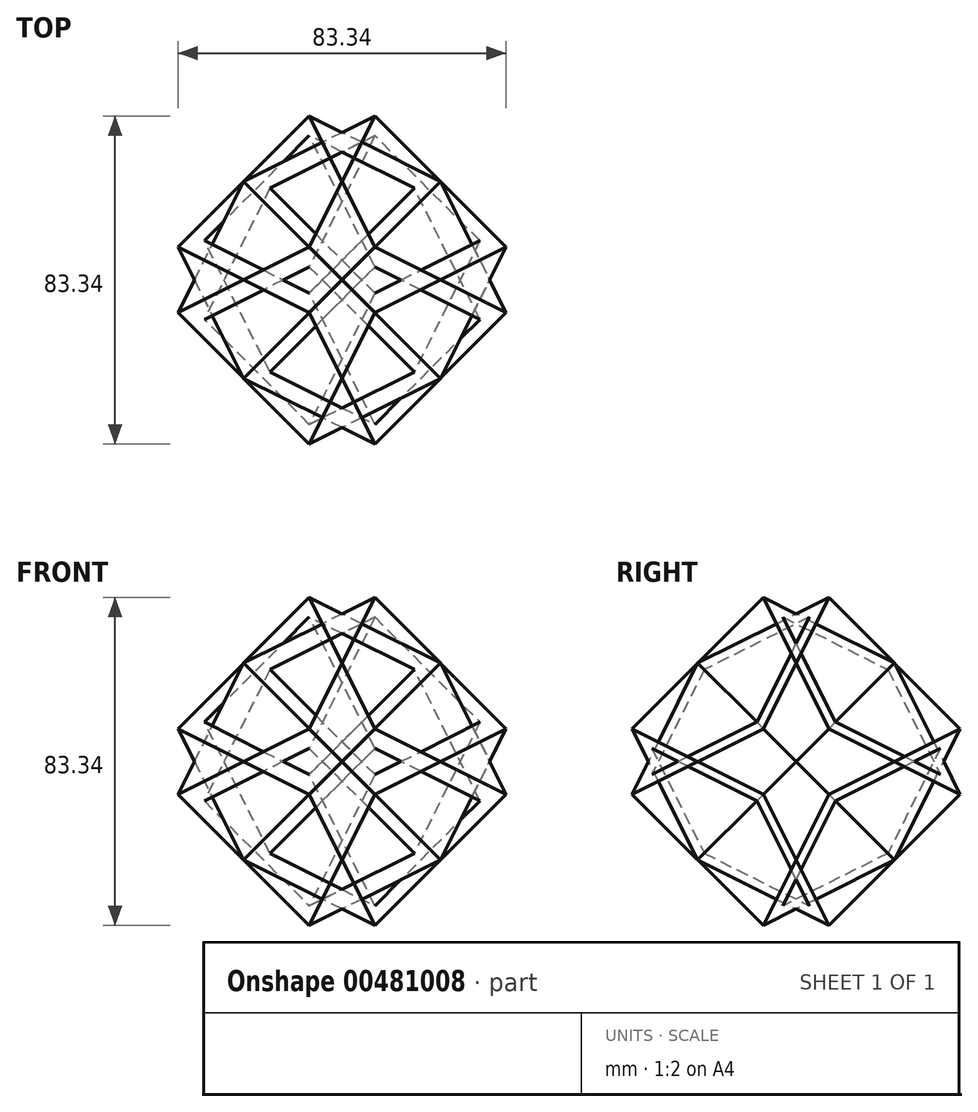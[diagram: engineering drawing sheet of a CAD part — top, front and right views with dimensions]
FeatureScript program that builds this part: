
annotation { "Feature Type Name" : "Feature", "Feature Type Description" : "" }
export const myFeature = defineFeature(function(context is Context, id is Id, definition is map)
    precondition{}
    {
        {
            var Q0;
            Q0=qCreatedBy(makeId("Front.planeOp"),FACE);
            var sketch = newSketch(context, id + "F0", { "sketchPlane" : qUnion([Q0])});
            skLineSegment(sketch, "E0.bottom", {"start": v(25, 25) * mm, "end": v(-25, 25) * mm});
            skLineSegment(sketch, "E0.top", {"start": v(25, -25) * mm, "end": v(-25, -25) * mm});
            skLineSegment(sketch, "E0.left", {"start": v(25, 25) * mm, "end": v(25, -25) * mm});
            skLineSegment(sketch, "E0.right", {"start": v(-25, 25) * mm, "end": v(-25, -25) * mm});
            skPoint(sketch, "E0.middle", {"position": v(0, 0) * mm});
            skSolve(sketch);
        }
        {
            var Q0;
            Q0=makeQuery(id+"F0.imprint","IMPRINT",FACE,{"disambiguationData":[TD([[makeQuery(id+"F0.imprint","IMPRINT",EDGE,{"derivedFrom":sQuery(id+"F0.wireOp",EDGE,"E0.bottom")}),1.0]])]});
            extrude(context, id + "F1", {"entities" : qUnion([Q0]), "endBound" : BoundingType.SYMMETRIC, "depth" : 50 * mm});
        }
        {
            var Q0;
            Q0=makeQuery(id+"F1.opExtrude","CAP_VERTEX",VERTEX,{"disambiguationData":[OSD([sQuery(id+"F0.wireOp",EDGE,"E0.bottom"),sQuery(id+"F0.wireOp",EDGE,"E0.left")])],"isStart":false});
            var Q1;
            Q1=makeQuery(id+"F1.opExtrude","CAP_VERTEX",VERTEX,{"disambiguationData":[OSD([sQuery(id+"F0.wireOp",EDGE,"E0.top"),sQuery(id+"F0.wireOp",EDGE,"E0.left")])],"isStart":false});
            var Q2;
            Q2=makeQuery(id+"F1.opExtrude","CAP_VERTEX",VERTEX,{"disambiguationData":[OSD([sQuery(id+"F0.wireOp",EDGE,"E0.top"),sQuery(id+"F0.wireOp",EDGE,"E0.right")])],"isStart":true});
            cPlane(context, id + "F2", {"entities" : qUnion([Q0, Q1, Q2]), "cplaneType" : CPlaneType.THREE_POINT, "offset" : 25 * mm, "width" : 150 * mm, "height" : 150 * mm});
        }
        {
            var Q0;
            Q0=qCreatedBy(id+"F2.planeOp",FACE);
            var sketch = newSketch(context, id + "F3", { "sketchPlane" : qUnion([Q0])});
            skLineSegment(sketch, "E1", {"start": v(-46.2, -32.67) * mm, "end": v(57, 40.3) * mm, "construction": true});
            skSolve(sketch);
        }
        {
            var Q0;
            Q0=makeQuery(id+"F1.opExtrude","SWEPT_BODY",BODY,{"disambiguationData":[OSD([sQuery(id+"F0.wireOp",EDGE,"E0.bottom"),sQuery(id+"F0.wireOp",EDGE,"E0.top"),sQuery(id+"F0.wireOp",EDGE,"E0.left"),sQuery(id+"F0.wireOp",EDGE,"E0.right")])]});
            var Q1;
            Q1=sQuery(id+"F3.wireOp",EDGE,"E1");
            transform(context, id + "F4", {"entities" : qUnion([Q0]), "transformType" : TransformType.ROTATION, "transformAxis" : qUnion([Q1]), "angle" : 60 * degree, "makeCopy" : false});
        }
        {
            var Q0;
            Q0=qCreatedBy(makeId("Front.planeOp"),FACE);
            var sketch = newSketch(context, id + "F5", { "sketchPlane" : qUnion([Q0])});
            skLineSegment(sketch, "E2", {"start": v(-43.87, 0) * mm, "end": v(62.3, 0) * mm, "construction": true});
            skSolve(sketch);
        }
        {
            var Q0;
            Q0=makeQuery(id+"F1.opExtrude","SWEPT_BODY",BODY,{"disambiguationData":[OSD([sQuery(id+"F0.wireOp",EDGE,"E0.bottom"),sQuery(id+"F0.wireOp",EDGE,"E0.top"),sQuery(id+"F0.wireOp",EDGE,"E0.left"),sQuery(id+"F0.wireOp",EDGE,"E0.right")])]});
            var Q1;
            Q1=sQuery(id+"F5.wireOp",EDGE,"E2");
            transform(context, id + "F6", {"entities" : qUnion([Q0]), "transformType" : TransformType.ROTATION, "transformAxis" : qUnion([Q1]), "angle" : 90 * degree, "makeCopy" : true});
        }
        {
            var Q0;
            Q0=makeQuery(id+"F1.opExtrude","SWEPT_BODY",BODY,{"disambiguationData":[OSD([sQuery(id+"F0.wireOp",EDGE,"E0.bottom"),sQuery(id+"F0.wireOp",EDGE,"E0.top"),sQuery(id+"F0.wireOp",EDGE,"E0.left"),sQuery(id+"F0.wireOp",EDGE,"E0.right")])]});
            var Q1;
            Q1=sQuery(id+"F5.wireOp",EDGE,"E2");
            transform(context, id + "F7", {"entities" : qUnion([Q0]), "transformType" : TransformType.ROTATION, "transformAxis" : qUnion([Q1]), "angle" : 270 * degree, "makeCopy" : true});
        }
        {
            var Q0;
            Q0=makeQuery(id+"F1.opExtrude","SWEPT_BODY",BODY,{"disambiguationData":[OSD([sQuery(id+"F0.wireOp",EDGE,"E0.bottom"),sQuery(id+"F0.wireOp",EDGE,"E0.top"),sQuery(id+"F0.wireOp",EDGE,"E0.left"),sQuery(id+"F0.wireOp",EDGE,"E0.right")])]});
            var Q1;
            Q1=sQuery(id+"F5.wireOp",EDGE,"E2");
            transform(context, id + "F8", {"entities" : qUnion([Q0]), "transformType" : TransformType.ROTATION, "transformAxis" : qUnion([Q1]), "angle" : 180 * degree, "makeCopy" : true});
        }
        {
            var Q0;
            Q0=makeQuery(id+"F1.opExtrude","CAP_FACE",FACE,{"disambiguationData":[OSD([sQuery(id+"F0.wireOp",EDGE,"E0.bottom"),sQuery(id+"F0.wireOp",EDGE,"E0.top"),sQuery(id+"F0.wireOp",EDGE,"E0.left"),sQuery(id+"F0.wireOp",EDGE,"E0.right")])],"isStart":false});
            var sketch = newSketch(context, id + "F9", { "sketchPlane" : qUnion([Q0])});
            skLineSegment(sketch, "E3.0", {"start": v(8.94, -26.83) * mm, "end": v(26.83, 8.94) * mm});
            skLineSegment(sketch, "E3.1", {"start": v(-26.83, -8.94) * mm, "end": v(8.94, -26.83) * mm});
            skLineSegment(sketch, "E3.2", {"start": v(-8.94, 26.83) * mm, "end": v(-26.83, -8.94) * mm});
            skLineSegment(sketch, "E3.3", {"start": v(26.83, 8.94) * mm, "end": v(-8.94, 26.83) * mm});
            skSolve(sketch);
        }
        {
            var Q0;
            Q0=makeQuery(id+"F9.imprint","IMPRINT",FACE,{"disambiguationData":[TD([[makeQuery(id+"F9.imprint","IMPRINT",EDGE,{"derivedFrom":sQuery(id+"F9.wireOp",EDGE,"E3.0")}),1.0]])]});
            extrude(context, id + "F10", {"entities" : qUnion([Q0]), "operationType" : NewBodyOperationType.REMOVE, "endBound" : BoundingType.THROUGH_ALL, "oppositeDirection" : true, "depth" : 25 * mm});
        }
        {
            var Q0;
            Q0=makeQuery(id+"F1.opExtrude","SWEPT_FACE",FACE,{"disambiguationData":[OSD([sQuery(id+"F0.wireOp",EDGE,"E0.bottom")])]});
            var sketch = newSketch(context, id + "F11", { "sketchPlane" : qUnion([Q0])});
            skLineSegment(sketch, "E4.0", {"start": v(0, 28.28) * mm, "end": v(-28.28, 0) * mm});
            skLineSegment(sketch, "E4.1", {"start": v(28.28, 0) * mm, "end": v(0, 28.28) * mm});
            skLineSegment(sketch, "E4.2", {"start": v(0, -28.28) * mm, "end": v(28.28, 0) * mm});
            skLineSegment(sketch, "E4.3", {"start": v(-28.28, 0) * mm, "end": v(0, -28.28) * mm});
            skSolve(sketch);
        }
        {
            var Q0;
            Q0=makeQuery(id+"F11.imprint","IMPRINT",FACE,{"disambiguationData":[TD([[makeQuery(id+"F11.imprint","IMPRINT",EDGE,{"derivedFrom":sQuery(id+"F11.wireOp",EDGE,"E4.0")}),1.0]])]});
            extrude(context, id + "F12", {"entities" : qUnion([Q0]), "operationType" : NewBodyOperationType.REMOVE, "endBound" : BoundingType.THROUGH_ALL, "oppositeDirection" : true, "depth" : 25 * mm});
        }
        {
            var Q0;
            Q0=makeQuery(id+"F1.opExtrude","SWEPT_FACE",FACE,{"disambiguationData":[OSD([sQuery(id+"F0.wireOp",EDGE,"E0.left")])]});
            var sketch = newSketch(context, id + "F13", { "sketchPlane" : qUnion([Q0])});
            skLineSegment(sketch, "E5.0", {"start": v(-8.94, 26.83) * mm, "end": v(-26.83, -8.94) * mm});
            skLineSegment(sketch, "E5.1", {"start": v(26.83, 8.94) * mm, "end": v(-8.94, 26.83) * mm});
            skLineSegment(sketch, "E5.2", {"start": v(8.94, -26.83) * mm, "end": v(26.83, 8.94) * mm});
            skLineSegment(sketch, "E5.3", {"start": v(-26.83, -8.94) * mm, "end": v(8.94, -26.83) * mm});
            skSolve(sketch);
        }
        {
            var Q0;
            Q0=makeQuery(id+"F13.imprint","IMPRINT",FACE,{"disambiguationData":[TD([[makeQuery(id+"F13.imprint","IMPRINT",EDGE,{"derivedFrom":sQuery(id+"F13.wireOp",EDGE,"E5.0")}),1.0]])]});
            extrude(context, id + "F14", {"entities" : qUnion([Q0]), "operationType" : NewBodyOperationType.REMOVE, "endBound" : BoundingType.THROUGH_ALL, "oppositeDirection" : true, "depth" : 25 * mm});
        }
        {
            var Q0;
            Q0=makeQuery(id+"F6.opPattern","COPY",BODY,{"derivedFrom":makeQuery(id+"F1.opExtrude","SWEPT_BODY",BODY,{"disambiguationData":[OSD([sQuery(id+"F0.wireOp",EDGE,"E0.bottom"),sQuery(id+"F0.wireOp",EDGE,"E0.top"),sQuery(id+"F0.wireOp",EDGE,"E0.left"),sQuery(id+"F0.wireOp",EDGE,"E0.right")])]}),"instanceName":"1"});
            var Q1;
            Q1=makeQuery(id+"F7.opPattern","COPY",BODY,{"derivedFrom":makeQuery(id+"F1.opExtrude","SWEPT_BODY",BODY,{"disambiguationData":[OSD([sQuery(id+"F0.wireOp",EDGE,"E0.bottom"),sQuery(id+"F0.wireOp",EDGE,"E0.top"),sQuery(id+"F0.wireOp",EDGE,"E0.left"),sQuery(id+"F0.wireOp",EDGE,"E0.right")])]}),"instanceName":"1"});
            var Q2;
            Q2=makeQuery(id+"F8.opPattern","COPY",BODY,{"derivedFrom":makeQuery(id+"F1.opExtrude","SWEPT_BODY",BODY,{"disambiguationData":[OSD([sQuery(id+"F0.wireOp",EDGE,"E0.bottom"),sQuery(id+"F0.wireOp",EDGE,"E0.top"),sQuery(id+"F0.wireOp",EDGE,"E0.left"),sQuery(id+"F0.wireOp",EDGE,"E0.right")])]}),"instanceName":"1"});
            deleteBodies(context, id + "F15", {"entities" : qUnion([Q0, Q1, Q2])});
        }
        {
            var Q0;
            Q0=makeQuery(id+"F1.opExtrude","SWEPT_BODY",BODY,{"disambiguationData":[OSD([sQuery(id+"F0.wireOp",EDGE,"E0.bottom"),sQuery(id+"F0.wireOp",EDGE,"E0.top"),sQuery(id+"F0.wireOp",EDGE,"E0.left"),sQuery(id+"F0.wireOp",EDGE,"E0.right")])]});
            var Q1;
            Q1=sQuery(id+"F5.wireOp",EDGE,"E2");
            transform(context, id + "F16", {"entities" : qUnion([Q0]), "transformType" : TransformType.ROTATION, "transformAxis" : qUnion([Q1]), "angle" : 90 * degree, "makeCopy" : true});
        }
        {
            var Q0;
            Q0=makeQuery(id+"F1.opExtrude","SWEPT_BODY",BODY,{"disambiguationData":[OSD([sQuery(id+"F0.wireOp",EDGE,"E0.bottom"),sQuery(id+"F0.wireOp",EDGE,"E0.top"),sQuery(id+"F0.wireOp",EDGE,"E0.left"),sQuery(id+"F0.wireOp",EDGE,"E0.right")])]});
            var Q1;
            Q1=sQuery(id+"F5.wireOp",EDGE,"E2");
            transform(context, id + "F17", {"entities" : qUnion([Q0]), "transformType" : TransformType.ROTATION, "transformAxis" : qUnion([Q1]), "angle" : 180 * degree, "makeCopy" : true});
        }
        {
            var Q0;
            Q0=makeQuery(id+"F1.opExtrude","SWEPT_BODY",BODY,{"disambiguationData":[OSD([sQuery(id+"F0.wireOp",EDGE,"E0.bottom"),sQuery(id+"F0.wireOp",EDGE,"E0.top"),sQuery(id+"F0.wireOp",EDGE,"E0.left"),sQuery(id+"F0.wireOp",EDGE,"E0.right")])]});
            var Q1;
            Q1=sQuery(id+"F5.wireOp",EDGE,"E2");
            transform(context, id + "F18", {"entities" : qUnion([Q0]), "transformType" : TransformType.ROTATION, "transformAxis" : qUnion([Q1]), "angle" : 270 * degree, "makeCopy" : true});
        }
    });
